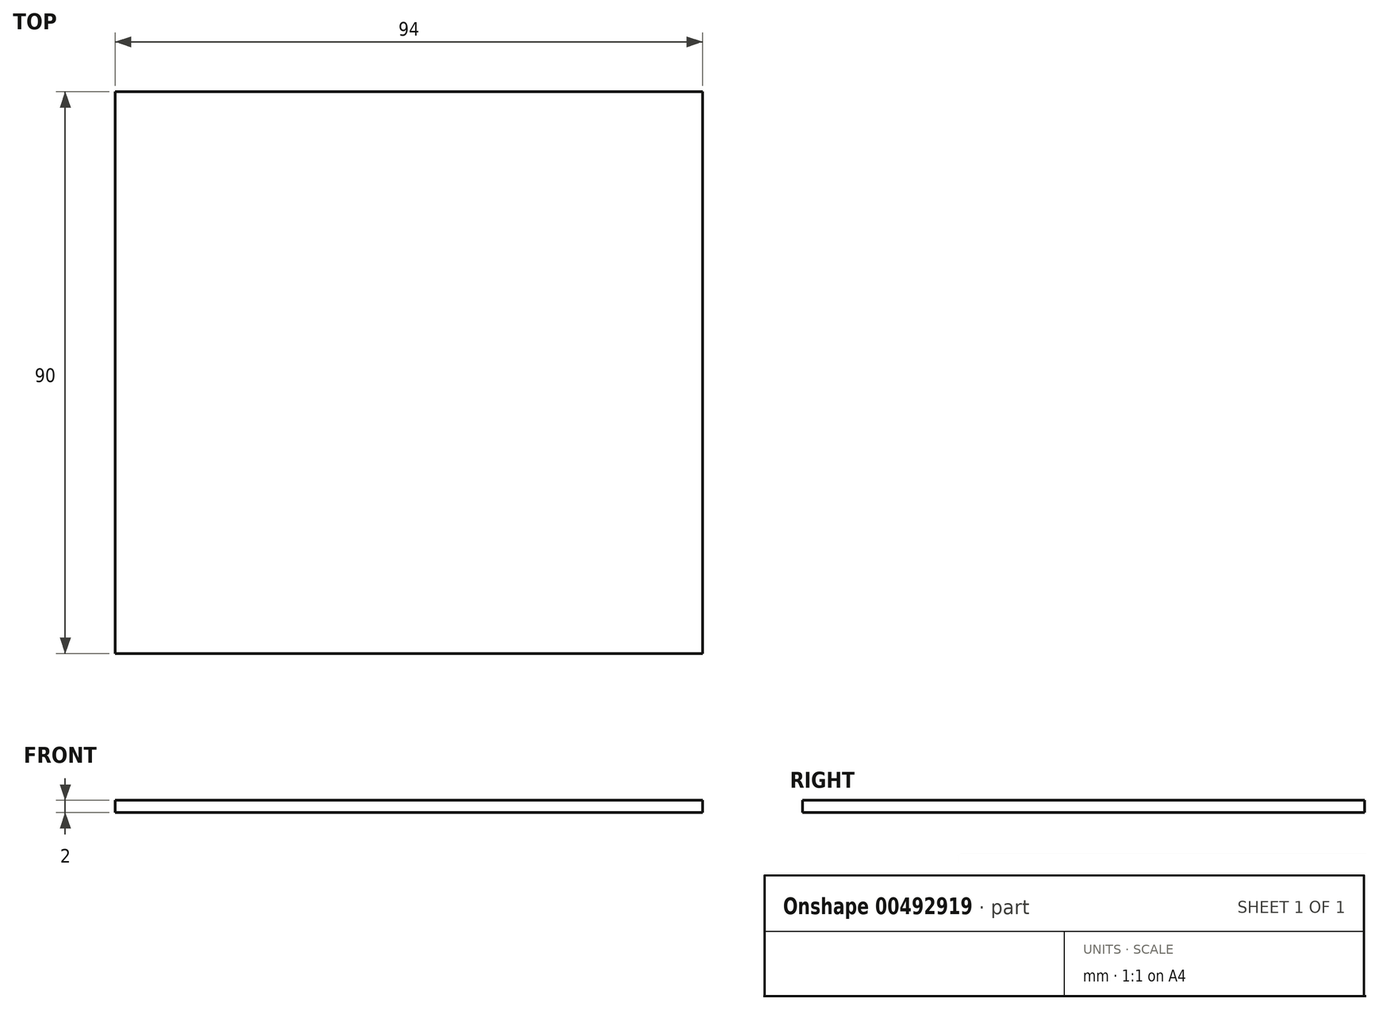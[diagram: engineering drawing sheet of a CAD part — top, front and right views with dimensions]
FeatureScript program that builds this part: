
annotation { "Feature Type Name" : "Feature", "Feature Type Description" : "" }
export const myFeature = defineFeature(function(context is Context, id is Id, definition is map)
    precondition{}
    {
        {
            var Q0;
            Q0=qCreatedBy(makeId("Top.planeOp"),FACE);
            var sketch = newSketch(context, id + "F0", { "sketchPlane" : qUnion([Q0])});
            skLineSegment(sketch, "E0.bottom", {"start": v(47, 45) * mm, "end": v(-47, 45) * mm});
            skLineSegment(sketch, "E0.top", {"start": v(47, -45) * mm, "end": v(-47, -45) * mm});
            skLineSegment(sketch, "E0.left", {"start": v(47, 45) * mm, "end": v(47, -45) * mm});
            skLineSegment(sketch, "E0.right", {"start": v(-47, 45) * mm, "end": v(-47, -45) * mm});
            skPoint(sketch, "E0.middle", {"position": v(0, 0) * mm});
            skSolve(sketch);
        }
        {
            var Q0;
            Q0=makeQuery(id+"F0.imprint","IMPRINT",FACE,{"disambiguationData":[TD([[makeQuery(id+"F0.imprint","IMPRINT",EDGE,{"derivedFrom":sQuery(id+"F0.wireOp",EDGE,"E0.bottom")}),1.0]])]});
            extrude(context, id + "F1", {"entities" : qUnion([Q0]), "depth" : 2 * mm, "offsetDistance" : 25 * mm});
        }
    });
